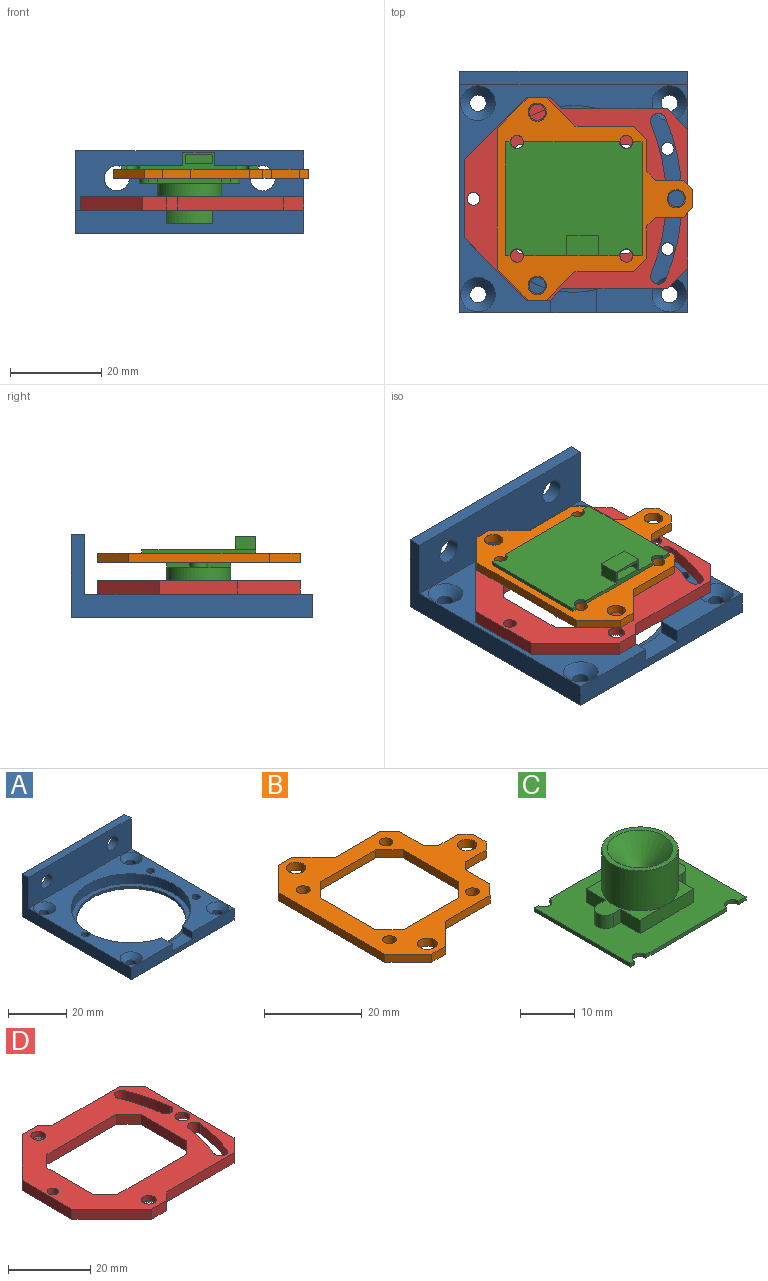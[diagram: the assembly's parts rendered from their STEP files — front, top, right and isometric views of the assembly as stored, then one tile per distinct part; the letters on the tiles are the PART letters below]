
ASSEMBLY  parts=4 mates=7
PART A: 27 faces, bbox 50x53x18 mm
  f0: plane 50x50mm, normal (0,0,1), area 932.8mm2, adj f2,f4,f5,f6,f8,f9,f15,f16
  f1: plane 53x50mm, normal (0,0,-1), area 1486.3mm2, adj f2,f3,f4,f5,f11,f12,f13,f14
  f2: plane 50x5mm, normal (0,-1,0), area 220mm2, adj f0,f1,f4,f5,f8,f9,f10
  f3: cylinder r=18.75mm len=37.5mm, axis (0,0,-1), area 117.8mm2, adj f1,f7
  f4: plane 53x18mm, normal (1,0,0), area 304mm2, adj f0,f1,f2,f17,f18,f19
  f5: plane 53x18mm, normal (-1,0,0), area 304mm2, adj f0,f1,f2,f17,f18,f19
  f6: cylinder r=20.5mm len=41mm, axis (0,0,1), area 484.9mm2, adj f0,f7,f8,f9,f10
  f7: plane 41x41mm, normal (0,0,1), area 215.8mm2, adj f3,f6
  f8: plane 5.12x3mm, normal (1,0,0), area 15.4mm2, adj f0,f2,f6,f10
  f9: plane 5.12x3mm, normal (-1,0,0), area 15.4mm2, adj f0,f2,f6,f10
  f10: plane 10x5.12mm, normal (0,0,1), area 47.1mm2, adj f2,f6,f8,f9
  f11: cylinder r=1.8mm len=3.6mm, axis (0,0,1), area 33.9mm2, adj f1,f23
  f12: cylinder r=1.8mm len=3.6mm, axis (0,0,1), area 33.9mm2, adj f1,f24
  f13: cylinder r=1.8mm len=3.6mm, axis (0,0,1), area 33.9mm2, adj f1,f26
  f14: cylinder r=1.8mm len=3.6mm, axis (0,0,1), area 33.9mm2, adj f1,f25
  f15: cylinder r=1.4mm len=5mm, axis (0,0,1), area 44mm2, adj f0,f1
  f16: cylinder r=1.4mm len=5mm, axis (0,0,1), area 44mm2, adj f0,f1
  f17: plane 50x3mm, normal (0,0,1), area 150mm2, adj f4,f5,f18,f19
  f18: plane 50x18mm, normal (0,1,0), area 852.5mm2, adj f1,f4,f5,f17,f20,f21
  f19: plane 50x13mm, normal (0,-1,0), area 602.5mm2, adj f0,f4,f5,f17,f20,f21
  f20: cylinder r=2.75mm len=5.5mm, axis (0,1,0), area 51.8mm2, adj f18,f19
  f21: cylinder r=2.75mm len=5.5mm, axis (0,1,0), area 51.8mm2, adj f18,f19
  f22: cylinder r=1.4mm len=5mm, axis (0,0,1), area 44mm2, adj f0,f1
  f23: cone r=1.8mm half-angle=45deg, axis (0,0,1), area 49.8mm2, adj f0,f11
  f24: cone r=1.8mm half-angle=45deg, axis (0,0,1), area 49.8mm2, adj f0,f12
  f25: cone r=3.8mm half-angle=45deg, axis (0,0,1), area 49.8mm2, adj f0,f14
  f26: cone r=3.8mm half-angle=45deg, axis (0,0,1), area 49.8mm2, adj f0,f13
PART B: 37 faces, bbox 42.8x44.5x2 mm
  f0: plane 2x2mm, normal (0.71,0.71,0), area 5.7mm2, adj f1,f34,f35,f36
  f1: plane 6x2mm, normal (0,1,0), area 12mm2, adj f0,f2,f35,f36
  f2: plane 2x1.96mm, normal (0.71,0.71,0), area 5.5mm2, adj f1,f3,f35,f36
  f3: plane 7.11x2mm, normal (1,0,0), area 14.2mm2, adj f2,f4,f35,f36
  f4: plane 2.9x2.9mm, normal (0.71,0.71,0), area 8.2mm2, adj f3,f5,f35,f36
  f5: plane 12.86x2mm, normal (0,1,0), area 25.7mm2, adj f4,f6,f35,f36
  f6: plane 6.28x6.28mm, normal (0.71,0.71,0), area 17.8mm2, adj f5,f7,f35,f36
  f7: plane 4x2mm, normal (0,1,0), area 8mm2, adj f6,f8,f35,f36
  f8: plane 6.78x6.78mm, normal (-0.71,0.71,0), area 19.2mm2, adj f7,f9,f35,f36
  f9: plane 30.93x2mm, normal (-1,0,0), area 61.9mm2, adj f8,f10,f35,f36
  f10: plane 6.78x6.78mm, normal (-0.71,-0.71,0), area 19.2mm2, adj f9,f11,f35,f36
  f11: plane 4x2mm, normal (0,-1,0), area 8mm2, adj f10,f12,f35,f36
  f12: plane 6.28x6.28mm, normal (0.71,-0.71,0), area 17.8mm2, adj f11,f13,f35,f36
  f13: plane 12.86x2mm, normal (0,-1,0), area 25.7mm2, adj f12,f14,f35,f36
  f14: plane 2.9x2.9mm, normal (0.71,-0.71,0), area 8.2mm2, adj f13,f15,f35,f36
  f15: plane 7.11x2mm, normal (1,0,0), area 14.2mm2, adj f14,f16,f35,f36
  f16: plane 2x1.96mm, normal (0.71,-0.71,0), area 5.5mm2, adj f15,f17,f35,f36
  f17: plane 6x2mm, normal (0,-1,0), area 12mm2, adj f16,f18,f35,f36
  f18: plane 2x2mm, normal (0.71,-0.71,0), area 5.7mm2, adj f17,f34,f35,f36
  f19: plane 16x2mm, normal (0,1,0), area 32mm2, adj f20,f33,f35,f36
  f20: plane 4x4mm, normal (0.71,0.71,0), area 11.3mm2, adj f19,f21,f35,f36
  f21: plane 16x2mm, normal (1,0,0), area 32mm2, adj f20,f22,f35,f36
  f22: plane 4x4mm, normal (0.71,-0.71,0), area 11.3mm2, adj f21,f23,f35,f36
  f23: plane 16x2mm, normal (0,-1,0), area 32mm2, adj f22,f24,f35,f36
  f24: plane 4x4mm, normal (-0.71,-0.71,0), area 11.3mm2, adj f23,f25,f35,f36
  f25: plane 16x2mm, normal (-1,0,0), area 32mm2, adj f24,f33,f35,f36
  f26: cylinder r=1.4mm len=2.8mm, axis (0,0,-1), area 17.6mm2, adj f35,f36
  f27: cylinder r=1.4mm len=2.8mm, axis (0,0,-1), area 17.6mm2, adj f35,f36
  f28: cylinder r=1.4mm len=2.8mm, axis (0,0,-1), area 17.6mm2, adj f35,f36
  f29: cylinder r=1.4mm len=2.8mm, axis (0,0,-1), area 17.6mm2, adj f35,f36
  f30: cylinder r=2mm len=4mm, axis (0,0,-1), area 25.1mm2, adj f35,f36
  f31: cylinder r=2mm len=4mm, axis (0,0,-1), area 25.1mm2, adj f35,f36
  f32: cylinder r=2mm len=4mm, axis (0,0,-1), area 25.1mm2, adj f35,f36
  f33: plane 4x4mm, normal (-0.71,0.71,0), area 11.3mm2, adj f19,f25,f35,f36
  f34: plane 4x2mm, normal (1,0,0), area 8mm2, adj f0,f18,f35,f36
  f35: plane 44.49x42.78mm, normal (0,0,1), area 641.8mm2, adj f0,f1,f2,f3,f4,f5,f6,f7
  f36: plane 44.49x42.78mm, normal (0,0,-1), area 641.8mm2, adj f0,f1,f2,f3,f4,f5,f6,f7
PART C: 42 faces, bbox 30x25x15.8 mm
  f0: plane 6x3mm, normal (0,0,1), area 18mm2, adj f1,f3,f4,f34
  f1: plane 3x2mm, normal (1,0,0), area 6mm2, adj f0,f2,f4,f34
  f2: plane 6x3mm, normal (0,0,-1), area 18mm2, adj f1,f3,f4,f34
  f3: plane 3x2mm, normal (-1,0,0), area 6mm2, adj f0,f2,f4,f34
  f4: plane 6x2mm, normal (0,1,0), area 12mm2, adj f0,f1,f2,f3
  f5: plane 4.5x3mm, normal (1,0,0), area 13.5mm2, adj f7,f8,f9,f34
  f6: plane 4.5x3mm, normal (-1,0,0), area 13.5mm2, adj f7,f8,f9,f34
  f7: plane 7x3mm, normal (0,-1,0), area 21mm2, adj f5,f6,f8,f9
  f8: plane 7x4.5mm, normal (0,0,-1), area 31.5mm2, adj f5,f6,f7,f34
  f9: plane 30x25mm, normal (0,0,-1), area 704.4mm2, adj f5,f6,f7,f29,f30,f31,f32,f33
  f10: cone r=3.5mm half-angle=45deg, axis (0,0,1), area 155.5mm2, adj f11,f12
  f11: cylinder r=1mm len=2mm, axis (0,0,-1), area 6.3mm2, adj f10,f13
  f12: plane 14x14mm, normal (0,0,1), area 40.8mm2, adj f10,f14
  f13: plane 2x2mm, normal (0,0,1), area 3.1mm2, adj f11
  f14: cylinder r=7mm len=14mm, axis (0,0,1), area 395.8mm2, adj f12,f15,f16
  f15: plane 14x11mm, normal (0,0,1), area 35.3mm2, adj f14,f17,f18,f19,f25,f26,f27,f28
  f16: plane 14x11mm, normal (0,0,1), area 35.3mm2, adj f14,f19,f20,f21,f22,f23,f24,f25
  f17: plane 3x2mm, normal (0,1,0), area 6mm2, adj f15,f18,f28,f41
  f18: plane 5x3mm, normal (-1,0,0), area 15mm2, adj f15,f17,f19,f41
  f19: plane 14x3mm, normal (0,1,0), area 42mm2, adj f15,f16,f18,f20,f41
  f20: plane 5x3mm, normal (1,0,0), area 15mm2, adj f16,f19,f21,f41
  f21: plane 3x2mm, normal (0,1,0), area 6mm2, adj f16,f20,f22,f41
  f22: cylinder r=2mm len=4mm, axis (0,0,1), area 18.8mm2, adj f16,f21,f23,f41
  f23: plane 3x2mm, normal (0,-1,0), area 6mm2, adj f16,f22,f24,f41
  f24: plane 5x3mm, normal (1,0,0), area 15mm2, adj f16,f23,f25,f41
  f25: plane 14x3mm, normal (0,-1,0), area 42mm2, adj f15,f16,f24,f26,f41
  f26: plane 5x3mm, normal (-1,0,0), area 15mm2, adj f15,f25,f27,f41
  f27: plane 3x2mm, normal (0,-1,0), area 6mm2, adj f15,f26,f28,f41
  f28: cylinder r=2mm len=4mm, axis (0,0,1), area 18.8mm2, adj f15,f17,f27,f41
  f29: cylinder r=1.5mm len=3mm, axis (0,0,1), area 3.8mm2, adj f9,f30,f40,f41
  f30: plane 1.04x0.8mm, normal (0,-1,0), area 0.8mm2, adj f9,f29,f31,f41
  f31: plane 25x0.8mm, normal (-1,0,0), area 20mm2, adj f9,f30,f32,f41
  f32: plane 1.04x0.8mm, normal (0,1,0), area 0.8mm2, adj f9,f31,f33,f41
  f33: cylinder r=1.5mm len=3mm, axis (0,0,1), area 3.8mm2, adj f9,f32,f34,f41
  f34: plane 21x3.8mm, normal (0,1,0), area 25.8mm2, adj f0,f1,f2,f3,f5,f6,f8,f9
  f35: cylinder r=1.5mm len=3mm, axis (0,0,1), area 3.8mm2, adj f9,f34,f36,f41
  f36: plane 1.96x0.8mm, normal (0,1,0), area 1.6mm2, adj f9,f35,f37,f41
  f37: plane 25x0.8mm, normal (1,0,0), area 20mm2, adj f9,f36,f38,f41
  f38: plane 1.96x0.8mm, normal (0,-1,0), area 1.6mm2, adj f9,f37,f39,f41
  f39: cylinder r=1.5mm len=3mm, axis (0,0,1), area 3.8mm2, adj f9,f38,f40,f41
  f40: plane 21x0.8mm, normal (0,-1,0), area 16.8mm2, adj f9,f29,f39,f41
  f41: plane 30x25mm, normal (0,0,1), area 511.3mm2, adj f17,f18,f19,f20,f21,f22,f23,f24
PART D: 37 faces, bbox 49.8x44.6x3 mm
  f0: plane 4x4mm, normal (0.71,-0.71,0), area 17mm2, adj f1,f31,f32,f33
  f1: plane 24x3mm, normal (0,-1,0), area 72mm2, adj f0,f2,f32,f33
  f2: plane 4x4mm, normal (-0.71,-0.71,0), area 17mm2, adj f1,f3,f32,f33
  f3: plane 16x3mm, normal (-1,0,0), area 48mm2, adj f2,f4,f32,f33
  f4: plane 4x4mm, normal (-0.71,0.71,0), area 17mm2, adj f3,f5,f32,f33
  f5: plane 24x3mm, normal (0,1,0), area 72mm2, adj f4,f6,f32,f33
  f6: plane 4x4mm, normal (0.71,0.71,0), area 17mm2, adj f5,f31,f32,f33
  f7: plane 30.45x3mm, normal (1,0,0), area 89.1mm2, adj f8,f24,f32,f33,f36
  f8: plane 4.48x4.48mm, normal (0.71,0.71,0), area 19mm2, adj f7,f9,f32,f33
  f9: plane 23.16x3mm, normal (0,1,0), area 69.5mm2, adj f8,f10,f32,f33
  f10: plane 3x2.54mm, normal (0.71,0.71,0), area 10.8mm2, adj f9,f11,f32,f33
  f11: plane 5.15x3mm, normal (0,1,0), area 15.4mm2, adj f10,f12,f32,f33,f35
  f12: plane 13.67x13.67mm, normal (-0.71,0.71,0), area 58mm2, adj f11,f13,f32,f33
  f13: plane 17.16x3mm, normal (-1,0,0), area 51.5mm2, adj f12,f14,f32,f33
  f14: plane 13.67x13.67mm, normal (-0.71,-0.71,0), area 58mm2, adj f13,f15,f32,f33
  f15: plane 5.15x3mm, normal (0,-1,0), area 15.4mm2, adj f14,f16,f32,f33,f34
  f16: plane 3x2.54mm, normal (0.71,-0.71,0), area 10.8mm2, adj f15,f17,f32,f33
  f17: plane 23.16x3mm, normal (0,-1,0), area 69.5mm2, adj f16,f24,f32,f33
  f18: cylinder r=1.75mm len=3.36mm, axis (0,0,-1), area 16.5mm2, adj f19,f29,f32,f33
  f19: cylinder r=42.25mm len=11.52mm, axis (0,0,-1), area 35.8mm2, adj f18,f20,f32,f33
  f20: cylinder r=1.75mm len=3.49mm, axis (0,0,-1), area 16.5mm2, adj f19,f29,f32,f33
  f21: cylinder r=1.75mm len=3.36mm, axis (0,0,-1), area 16.5mm2, adj f22,f30,f32,f33
  f22: cylinder r=45.75mm len=12.48mm, axis (0,0,-1), area 38.8mm2, adj f21,f23,f32,f33
  f23: cylinder r=1.75mm len=3.49mm, axis (0,0,-1), area 16.5mm2, adj f22,f30,f32,f33
  f24: plane 4.48x4.48mm, normal (0.71,-0.71,0), area 19mm2, adj f7,f17,f32,f33
  f25: cylinder r=1.8mm len=3.6mm, axis (0,0,-1), area 17mm2, adj f32,f35
  f26: cylinder r=1.8mm len=3.6mm, axis (0,0,-1), area 17mm2, adj f32,f34
  f27: cylinder r=1.8mm len=3.6mm, axis (0,0,-1), area 17mm2, adj f32,f36
  f28: cylinder r=1.4mm len=3mm, axis (0,0,-1), area 26.4mm2, adj f32,f33
  f29: cylinder r=45.75mm len=12.48mm, axis (0,0,-1), area 38.8mm2, adj f18,f20,f32,f33
  f30: cylinder r=42.25mm len=11.52mm, axis (0,0,-1), area 35.8mm2, adj f21,f23,f32,f33
  f31: plane 16x3mm, normal (1,0,0), area 48mm2, adj f0,f6,f32,f33
  f32: plane 49x44.49mm, normal (0,0,1), area 947.3mm2, adj f0,f1,f2,f3,f4,f5,f6,f7
  f33: plane 49x44.49mm, normal (0,0,-1), area 877.7mm2, adj f0,f1,f2,f3,f4,f5,f6,f7
  f34: cone r=3.3mm half-angle=45deg, axis (0,0,-1), area 33.9mm2, adj f15,f26,f33
  f35: cone r=3.3mm half-angle=45deg, axis (0,0,-1), area 33.9mm2, adj f11,f25,f33
  f36: cone r=3.3mm half-angle=45deg, axis (0,0,-1), area 30.7mm2, adj f7,f27,f33
PLACE A at identity fixed
PLACE B rot(axis=(-0.74,0.67,0),0deg) t=(0,0,-13.81)mm
PLACE C rot(axis=(1,0,0),180deg) t=(0,0,14.77)mm
PLACE D rot(axis=(0,0,1),0.1deg) t=(0,0.02,5)mm
MATE cylindrical C.f10 <-> A.f6  axis (0,0,-1) through (0,0,1.97)mm
MATE cylindrical D.f28 <-> A.f16  axis (0,0,1) through (-22,0,8)mm
MATE cylindrical C.f33 <-> B.f28  axis (0,0,1) through (-12.46,-12.5,14.77)mm
MATE planar B.f35 <-> C.f41  axis (0,0,1) through (16.04,-5.96,13.97)mm
MATE cylindrical C.f39 <-> B.f27  axis (0,0,1) through (11.54,12.5,14.77)mm
MATE parallel C.f37 <-> A.f4  axis (1,0,0) through (15,0,14.37)mm
MATE planar A.f0 <-> D.f33  axis (0,0,1) through (-0.13,1.14,5)mm
